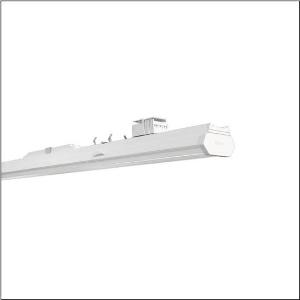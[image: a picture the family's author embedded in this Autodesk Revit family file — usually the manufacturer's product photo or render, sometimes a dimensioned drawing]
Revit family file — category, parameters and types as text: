
# Revit family: licross_r__11_protected_mo_51tp11dn495g_6ace
name_source: partatom
category: Lighting Fixtures
units: mm (PartAtom-declared; Revit-internal decimal feet)

## family parameters
Cut with Voids When Loaded = No
Host = Face
Light Source = No
Part Type = Normal
Room Calculation Point = No
Round Connector Dimension = Use Diameter
Shared = No

## types (1)
- --- (1 x LED, 9930 lm, 57.1 W, 4000K)
    Apparent Load = 57 VA
    CIE Flux Codes = 83 94 98 100 100
    Color Rendering = 80
    Color Temperature = 4000K
    Default Elevation = 1800 mm
    Description = Licross® 11 Protected MO, luminaire insert, of sheet steel, galvanised, coil coated, white, length: 1.500mm, width: 90mm, height: 101mm, LED rated luminous flux: 9.980lm, light colour: 840, control gear: DALI 2, with plug, 5-pole, with phase selection, mains connection: 220..240V, AC, 50/60Hz, rated input power: 57W, halogen-free wiring, primary light control with lens, of plastic, primary optical cover: cover, of PMMA, light emission: direct distribution, primary light characteristic: symmetric, protection rating (complete): IP64, insulation class (complete): insulation class I (protective earthing), certification: CE, ENEC, VDE, UKCA, protection symbol: D if used in an environment with conductive dust loads with corresponding accessories, impact resistance: IK06, permissible ambient temperature for indoor applications: -25..+35°C, corresponds to IFS (International Featured Standards) requirements for safety and quality in the food industry, reducing of maximum allowable ambient temperature of 5°C with ceiling mounting, LABS conformity tested according to VDMA 24364:2018-05, packaging unit: 1 piece
    Height = 92 mm
    Lamp = 1 x LED
    Lamp Light Flux = 9930 lm
    Lamp Power = 57.1 W
    Lamp count = 1
    Length = 1500 mm
    Luminous efficacy = 174 lm/W
    Manufacturer = Siteco
    ModVariant = No
    Model = 51TP11DN495G
    Mounting Place = Ceiling
    Mounting Type = Pendant
    Number of Poles = 1
    OnlyDefault = Yes
    Power Factor = 1
    Product Name = Licross® 11 Protected MO
    Product group = luminaire insert
    ProductGroupID = 901
    Protection Class = Protection class I
    Protection Degree = IP 64
    RLX_Detail_Level = 1
    RLX_Emergency_Light_Flux = 0 lm
    RLX_Emergency_Type = 0
    RLX_Emergency_Type_DB = No
    RlxData = <blob elided: 24073 chars, md5=a741fabb>
    Socket = socket
    Standby Power = 0 W
    System Light Flux = 9930 lm
    System Power = 57 W
    Type Comments = factory setting: luminous flux: 100 % | dim-lin: 254 | 378 mA
    Type Image = l_1256148.jpg
    URL = http://relux.com
    VarID = @adj_049215
    Voltage = 0 V
    Weight = 0.00 kg
    Width = 88 mm

## geometry (parser evidence)
native form markers: Blend x4, Sweep x10
no freeform markers — native parametric forms only
